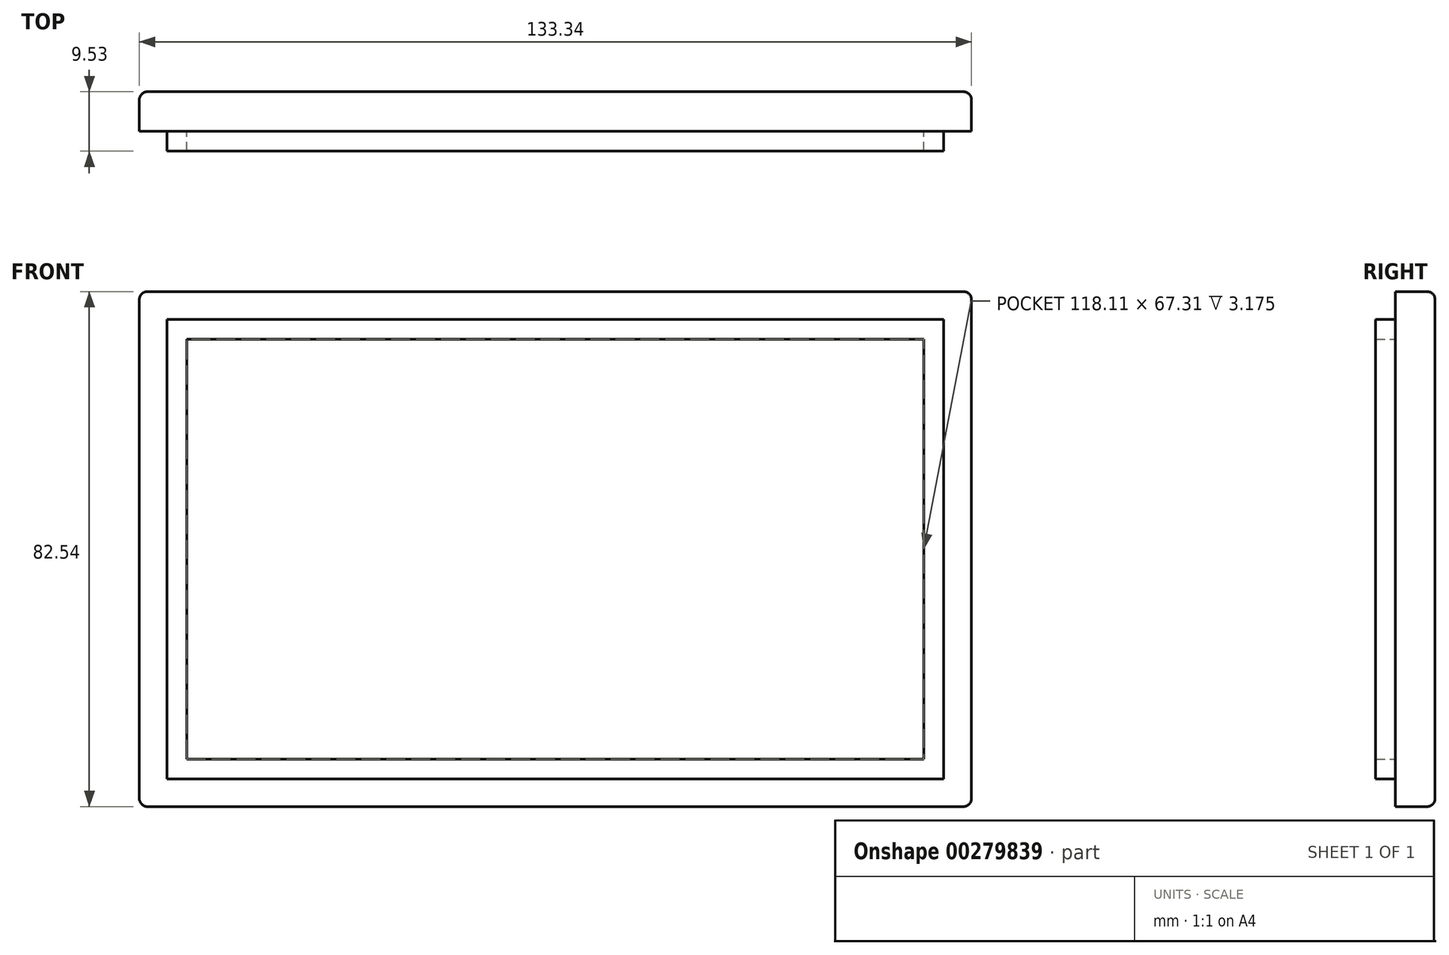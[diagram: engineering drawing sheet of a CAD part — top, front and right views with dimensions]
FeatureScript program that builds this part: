
annotation { "Feature Type Name" : "Feature", "Feature Type Description" : "" }
export const myFeature = defineFeature(function(context is Context, id is Id, definition is map)
    precondition{}
    {
        {
            var Q0;
            Q0=qCreatedBy(makeId("Front.planeOp"),FACE);
            var sketch = newSketch(context, id + "F0", { "sketchPlane" : qUnion([Q0])});
            skLineSegment(sketch, "E0.bottom", {"start": v(66.68, -41.28) * mm, "end": v(-66.68, -41.28) * mm});
            skLineSegment(sketch, "E0.top", {"start": v(66.68, 41.28) * mm, "end": v(-66.68, 41.27) * mm});
            skLineSegment(sketch, "E0.left", {"start": v(66.68, -41.28) * mm, "end": v(66.67, 41.28) * mm});
            skLineSegment(sketch, "E0.right", {"start": v(-66.68, -41.28) * mm, "end": v(-66.68, 41.27) * mm});
            skPoint(sketch, "E0.middle", {"position": v(0, 0) * mm});
            skLineSegment(sketch, "E1.bottom", {"start": v(62.23, -36.83) * mm, "end": v(-62.23, -36.83) * mm});
            skLineSegment(sketch, "E1.top", {"start": v(62.23, 36.83) * mm, "end": v(-62.23, 36.83) * mm});
            skLineSegment(sketch, "E1.left", {"start": v(62.23, -36.83) * mm, "end": v(62.23, 36.83) * mm});
            skLineSegment(sketch, "E1.right", {"start": v(-62.23, -36.83) * mm, "end": v(-62.23, 36.83) * mm});
            skLineSegment(sketch, "E2.bottom", {"start": v(59.06, -33.65) * mm, "end": v(-59.05, -33.66) * mm});
            skLineSegment(sketch, "E2.top", {"start": v(59.05, 33.66) * mm, "end": v(-59.06, 33.65) * mm});
            skLineSegment(sketch, "E2.left", {"start": v(59.06, -33.66) * mm, "end": v(59.05, 33.66) * mm});
            skLineSegment(sketch, "E2.right", {"start": v(-59.05, -33.66) * mm, "end": v(-59.06, 33.66) * mm});
            skSolve(sketch);
        }
        {
            var Q0;
            Q0=makeQuery(id+"F0.imprint","IMPRINT",FACE,{"disambiguationData":[TD([[makeQuery(id+"F0.imprint","IMPRINT",EDGE,{"derivedFrom":sQuery(id+"F0.wireOp",EDGE,"E0.bottom")}),-1.0]])]});
            var Q1;
            Q1=makeQuery(id+"F0.imprint","IMPRINT",FACE,{"disambiguationData":[TD([[makeQuery(id+"F0.imprint","IMPRINT",EDGE,{"derivedFrom":sQuery(id+"F0.wireOp",EDGE,"E1.bottom")}),-1.0]])]});
            var Q2;
            Q2=makeQuery(id+"F0.imprint","IMPRINT",FACE,{"disambiguationData":[TD([[makeQuery(id+"F0.imprint","IMPRINT",EDGE,{"derivedFrom":sQuery(id+"F0.wireOp",EDGE,"E2.bottom")}),-1.0]])]});
            extrude(context, id + "F1", {"entities" : qUnion([Q0, Q1, Q2]), "depth" : 6.35 * mm});
        }
        {
            var Q0;
            Q0=makeQuery(id+"F0.imprint","IMPRINT",FACE,{"disambiguationData":[TD([[makeQuery(id+"F0.imprint","IMPRINT",EDGE,{"derivedFrom":sQuery(id+"F0.wireOp",EDGE,"E1.bottom")}),-1.0]])]});
            extrude(context, id + "F2", {"entities" : qUnion([Q0]), "operationType" : NewBodyOperationType.ADD, "depth" : 9.52 * mm});
        }
        {
            var Q0;
            Q0=makeQuery(id+"F1.opExtrude","CAP_EDGE",EDGE,{"disambiguationData":[OSD([sQuery(id+"F0.wireOp",EDGE,"E0.bottom")])],"isStart":true});
            var Q1;
            Q1=makeQuery(id+"F1.opExtrude","CAP_EDGE",EDGE,{"disambiguationData":[OSD([sQuery(id+"F0.wireOp",EDGE,"E0.right")])],"isStart":true});
            var Q2;
            Q2=makeQuery(id+"F1.opExtrude","SWEPT_EDGE",EDGE,{"disambiguationData":[OSD([sQuery(id+"F0.wireOp",EDGE,"E0.bottom"),sQuery(id+"F0.wireOp",EDGE,"E0.right")])]});
            var Q3;
            Q3=makeQuery(id+"F1.opExtrude","SWEPT_EDGE",EDGE,{"disambiguationData":[OSD([sQuery(id+"F0.wireOp",EDGE,"E0.top"),sQuery(id+"F0.wireOp",EDGE,"E0.right")])]});
            var Q4;
            Q4=makeQuery(id+"F1.opExtrude","CAP_EDGE",EDGE,{"disambiguationData":[OSD([sQuery(id+"F0.wireOp",EDGE,"E0.top")])],"isStart":true});
            var Q5;
            Q5=makeQuery(id+"F1.opExtrude","SWEPT_EDGE",EDGE,{"disambiguationData":[OSD([sQuery(id+"F0.wireOp",EDGE,"E0.top"),sQuery(id+"F0.wireOp",EDGE,"E0.left")])]});
            var Q6;
            Q6=makeQuery(id+"F1.opExtrude","CAP_EDGE",EDGE,{"disambiguationData":[OSD([sQuery(id+"F0.wireOp",EDGE,"E0.left")])],"isStart":true});
            var Q7;
            Q7=makeQuery(id+"F1.opExtrude","SWEPT_EDGE",EDGE,{"disambiguationData":[OSD([sQuery(id+"F0.wireOp",EDGE,"E0.bottom"),sQuery(id+"F0.wireOp",EDGE,"E0.left")])]});
            fillet(context, id + "F3", {"entities" : qUnion([Q0, Q1, Q2, Q3, Q4, Q5, Q6, Q7]), "radius" : 1.27 * mm, "tangentPropagation" : true, "allowEdgeOverflow" : false});
        }
    });
